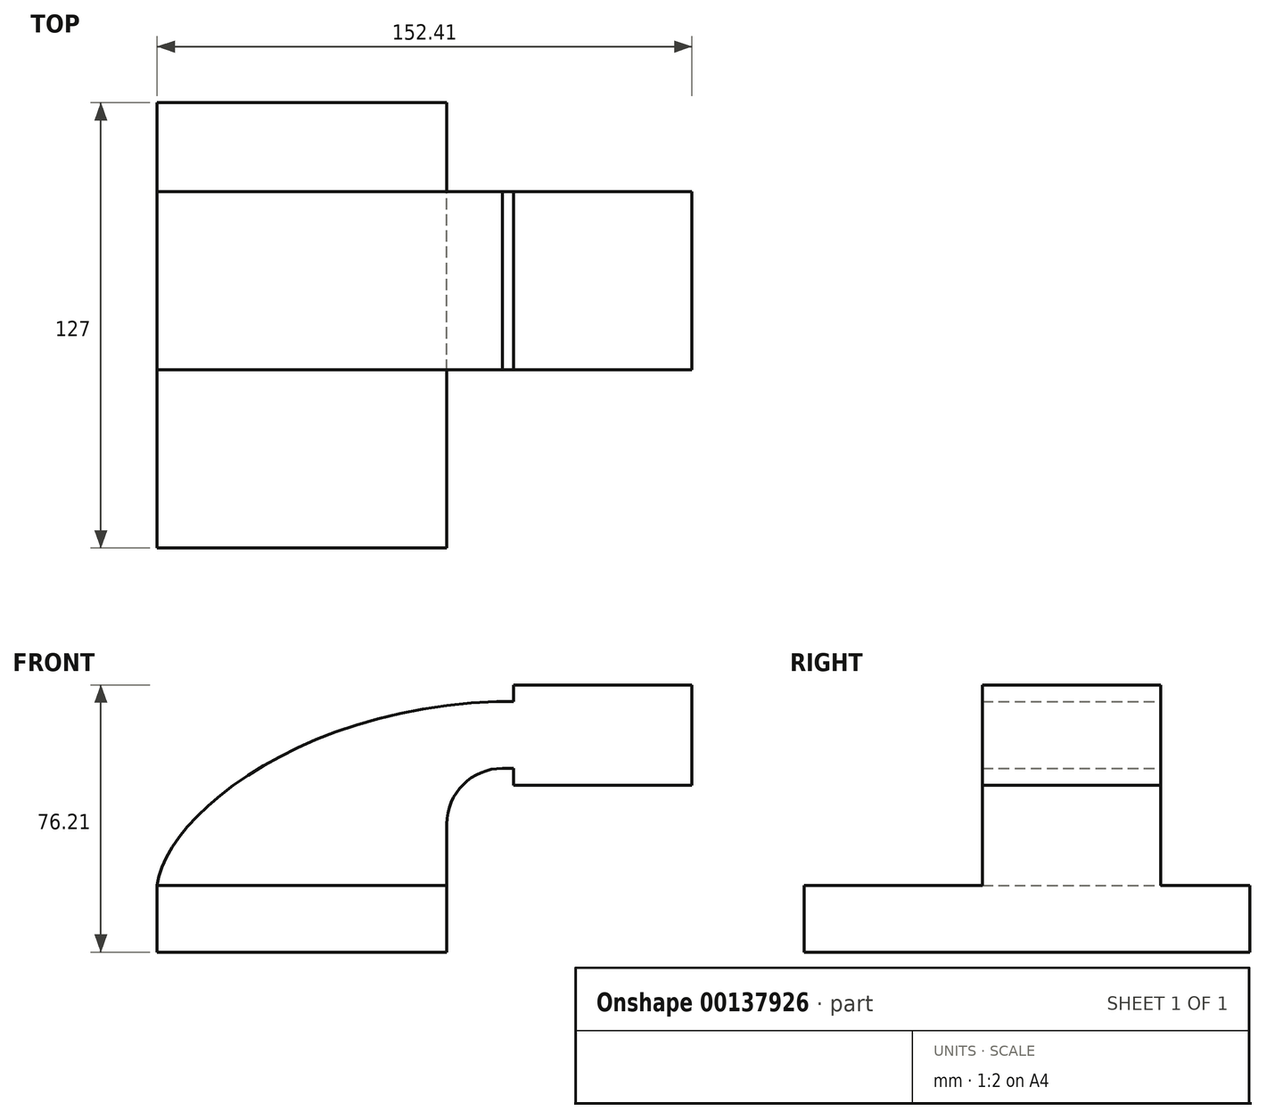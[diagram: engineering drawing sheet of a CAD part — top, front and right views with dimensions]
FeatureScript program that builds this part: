
annotation { "Feature Type Name" : "Feature", "Feature Type Description" : "" }
export const myFeature = defineFeature(function(context is Context, id is Id, definition is map)
    precondition{}
    {
        {
            var Q0;
            Q0=qCreatedBy(makeId("Front.planeOp"),FACE);
            var sketch = newSketch(context, id + "F0", { "sketchPlane" : qUnion([Q0])});
            skLineSegment(sketch, "E0.bottom", {"start": v(-41.28, -9.53) * mm, "end": v(41.28, -9.53) * mm});
            skLineSegment(sketch, "E0.top", {"start": v(-41.28, 9.52) * mm, "end": v(41.27, 9.52) * mm});
            skLineSegment(sketch, "E0.left", {"start": v(-41.27, -9.53) * mm, "end": v(-41.27, 9.52) * mm});
            skLineSegment(sketch, "E0.right", {"start": v(41.27, -9.53) * mm, "end": v(41.27, 9.52) * mm});
            skPoint(sketch, "E0.middle", {"position": v(0, 0) * mm});
            skLineSegment(sketch, "E1.bottom", {"start": v(60.32, 38.1) * mm, "end": v(111.12, 38.1) * mm});
            skLineSegment(sketch, "E1.top", {"start": v(60.32, 66.67) * mm, "end": v(111.12, 66.67) * mm});
            skLineSegment(sketch, "E1.left", {"start": v(60.32, 38.1) * mm, "end": v(60.32, 66.67) * mm});
            skLineSegment(sketch, "E1.right", {"start": v(111.12, 38.1) * mm, "end": v(111.12, 66.67) * mm});
            skPoint(sketch, "E1.middle", {"position": v(85.72, 52.39) * mm});
            skLineSegment(sketch, "E2", {"start": v(41.27, 9.52) * mm, "end": v(41.27, 27) * mm});
            skArc(sketch, "E3", {"start": v(41.27, 27) * mm, "mid": v(45.92, 38.23) * mm, "end": v(57.15, 42.88) * mm});
            skLineSegment(sketch, "E4", {"start": v(57.15, 42.88) * mm, "end": v(85.73, 42.88) * mm});
            skLineSegment(sketch, "E5.0", {"start": v(57.15, 61.93) * mm, "end": v(85.73, 61.93) * mm});
            skArc(sketch, "E5.1", {"start": v(22.22, 27) * mm, "mid": v(32.45, 51.7) * mm, "end": v(57.15, 61.93) * mm});
            skLineSegment(sketch, "E5.2", {"start": v(22.22, 9.52) * mm, "end": v(22.22, 27) * mm});
            skLineSegment(sketch, "E6", {"start": v(85.73, 61.93) * mm, "end": v(85.73, 42.88) * mm});
            skFitSpline(sketch, "E7", {"points": [v(-41.27, 9.52) * mm, v(57.15, 61.93) * mm], "startDerivative": vector(5.85, 57.5) * mm, "endDerivative": vector(171.45, 3.1) * mm});
            skSolve(sketch);
        }
        {
            var Q0;
            {var subQ3=sQuery(id+"F0.wireOp",EDGE,"E5.2");Q0=makeQuery(id+"F0.imprint","IMPRINT",FACE,{"disambiguationData":[TD([[makeQuery(id+"F0.imprint","IMPRINT",EDGE,{"derivedFrom":subQ3}),1.0]])]});}
            var Q1;
            {var subQ1=sQuery(id+"F0.wireOp",EDGE,"E2");Q1=makeQuery(id+"F0.imprint","IMPRINT",FACE,{"disambiguationData":[TD([[makeQuery(id+"F0.imprint","IMPRINT",EDGE,{"derivedFrom":subQ1}),1.0]])]});}
            var Q2;
            {var subQ5=sQuery(id+"F0.wireOp",EDGE,"E6");Q2=makeQuery(id+"F0.imprint","IMPRINT",FACE,{"disambiguationData":[TD([[makeQuery(id+"F0.imprint","IMPRINT",EDGE,{"derivedFrom":subQ5}),-1.0]])]});}
            var Q3;
            {var subQ4=sQuery(id+"F0.wireOp",EDGE,"E1.bottom");Q3=makeQuery(id+"F0.imprint","IMPRINT",FACE,{"disambiguationData":[TD([[makeQuery(id+"F0.imprint","IMPRINT",EDGE,{"derivedFrom":subQ4}),1.0]])]});}
            extrude(context, id + "F1", {"entities" : qUnion([Q0, Q1, Q2, Q3]), "endBound" : BoundingType.SYMMETRIC, "depth" : 50.8 * mm});
        }
        {
            var Q0;
            Q0 = qSketchRegion(id + "F0", true);
            extrude(context, id + "F2", {"entities" : qUnion([Q0]), "operationType" : NewBodyOperationType.ADD, "endBound" : BoundingType.SYMMETRIC, "depth" : 25.4 * mm});
        }
        {
            var Q0;
            Q0=makeQuery(id+"F2.opExtrude","CAP_FACE",FACE,{"disambiguationData":[OSD([sQuery(id+"F0.wireOp",EDGE,"E0.bottom"),sQuery(id+"F0.wireOp",EDGE,"E0.left"),sQuery(id+"F0.wireOp",EDGE,"E0.right"),sQuery(id+"F0.wireOp",EDGE,"E1.bottom"),sQuery(id+"F0.wireOp",EDGE,"E1.top"),sQuery(id+"F0.wireOp",EDGE,"E1.left"),sQuery(id+"F0.wireOp",EDGE,"E1.right"),sQuery(id+"F0.wireOp",EDGE,"E2"),sQuery(id+"F0.wireOp",EDGE,"E3"),sQuery(id+"F0.wireOp",EDGE,"E4"),sQuery(id+"F0.wireOp",EDGE,"E5.0"),sQuery(id+"F0.wireOp",EDGE,"E5.1"),sQuery(id+"F0.wireOp",EDGE,"E7")])],"isStart":false});
            extrude(context, id + "F3", {"entities" : qUnion([Q0]), "operationType" : NewBodyOperationType.ADD, "endBound" : BoundingType.SYMMETRIC, "depth" : 127 * mm});
        }
        {
            var Q0;
            Q0 = qSketchRegion(id + "F0", true);
            extrude(context, id + "F4", {"entities" : qUnion([Q0]), "operationType" : NewBodyOperationType.ADD, "endBound" : BoundingType.SYMMETRIC, "depth" : 25.4 * mm});
        }
        {
            var Q0;
            Q0 = qSketchRegion(id + "F0", true);
            extrude(context, id + "F5", {"entities" : qUnion([Q0]), "operationType" : NewBodyOperationType.ADD, "depth" : 25.4 * mm});
        }
    });
